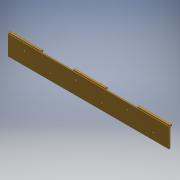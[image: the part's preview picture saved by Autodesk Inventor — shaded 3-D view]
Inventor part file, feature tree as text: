
AUTODESK INVENTOR PART (.ipt)
format: ipt  version: 2018 (Build 220112000, 112)  size: 165,888 bytes
history: native  units: mm
features: extrude x5, sketch x5, plane x1, hole x1
ambient origin geometry x8: Origin, YZ Plane, XZ Plane, XY Plane, X Axis, Y Axis, Z Axis, Center Point
bodies: Solid1 (feature_tree)
feature tree (12):
  extrude  "Extrusion1"  Depth=30.0mm
  sketch  "Sketch2"  dims[d2=2.0mm d3=0.0mm d4=2.5mm]
  extrude  "Extrusion2"  Depth=2.0mm
  extrude  "Extrusion3"  Depth=3.5mm
  sketch  "Sketch3"  dims[d5=3.0mm d6=3.5mm]
  plane  "Work Plane1"
  hole  "Hole1"  [1 undecoded]
  extrude  "Extrusion6"  Depth=10.0mm
  extrude  "Extrusion7"  Depth=10.0mm
  sketch  "Sketch1"  dims[d0=250.0mm d1=30.0mm]
  sketch  "Sketch5"  dims[d7=250.0mm d8=0.0mm d9=250.0mm d10=0.0mm]
  sketch  "Sketch6"  dims[d23=40.0mm d24=5.0mm d25=40.0mm d26=40.0mm d27=40.0mm d28=40.0mm d29=10.0mm d30=10.0mm d31=3.0mm d32=6.0mm d33=5.0mm d34=2.0mm d35=90.0deg d36=8.0mm d37=20.594885mm d38=50.0mm d39=2.75mm d40=50.0mm d41=2.75mm d42=50.0mm d43=50.0mm d44=250.0mm d45=0.0mm d46=10.0mm d47=0.0mm]
note: 1 required parameter value undecoded (feature->parameter linkage not recoverable at this tier; creation-order binding heuristic only, values carry confidence <= 0.55)
